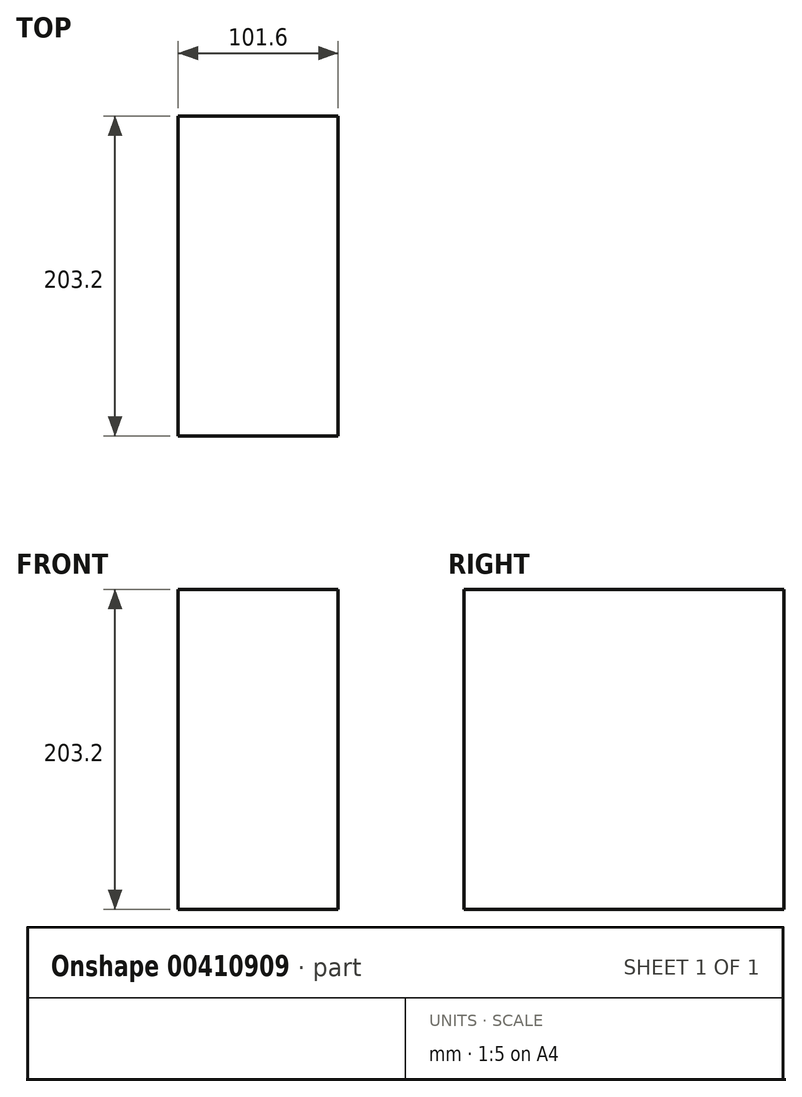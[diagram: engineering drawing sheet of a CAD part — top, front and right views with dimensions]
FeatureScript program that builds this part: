
annotation { "Feature Type Name" : "Feature", "Feature Type Description" : "" }
export const myFeature = defineFeature(function(context is Context, id is Id, definition is map)
    precondition{}
    {
        {
            var Q0;
            Q0=qCreatedBy(makeId("Top.planeOp"),FACE);
            var sketch = newSketch(context, id + "F0", { "sketchPlane" : qUnion([Q0])});
            skLineSegment(sketch, "E0", {"start": v(0, 0) * mm, "end": v(-101.6, 0) * mm});
            skLineSegment(sketch, "E1", {"start": v(-101.6, 0) * mm, "end": v(-101.6, 203.2) * mm});
            skLineSegment(sketch, "E2", {"start": v(-101.6, 203.2) * mm, "end": v(0, 203.2) * mm});
            skLineSegment(sketch, "E3", {"start": v(0, 203.2) * mm, "end": v(0, 0) * mm});
            skSolve(sketch);
        }
        {
            var Q0;
            Q0=makeQuery(id+"F0.imprint","IMPRINT",FACE,{"disambiguationData":[TD([[makeQuery(id+"F0.imprint","IMPRINT",EDGE,{"derivedFrom":sQuery(id+"F0.wireOp",EDGE,"E0")}),-1.0]])]});
            extrude(context, id + "F1", {"entities" : qUnion([Q0]), "depth" : 203.2 * mm});
        }
    });
